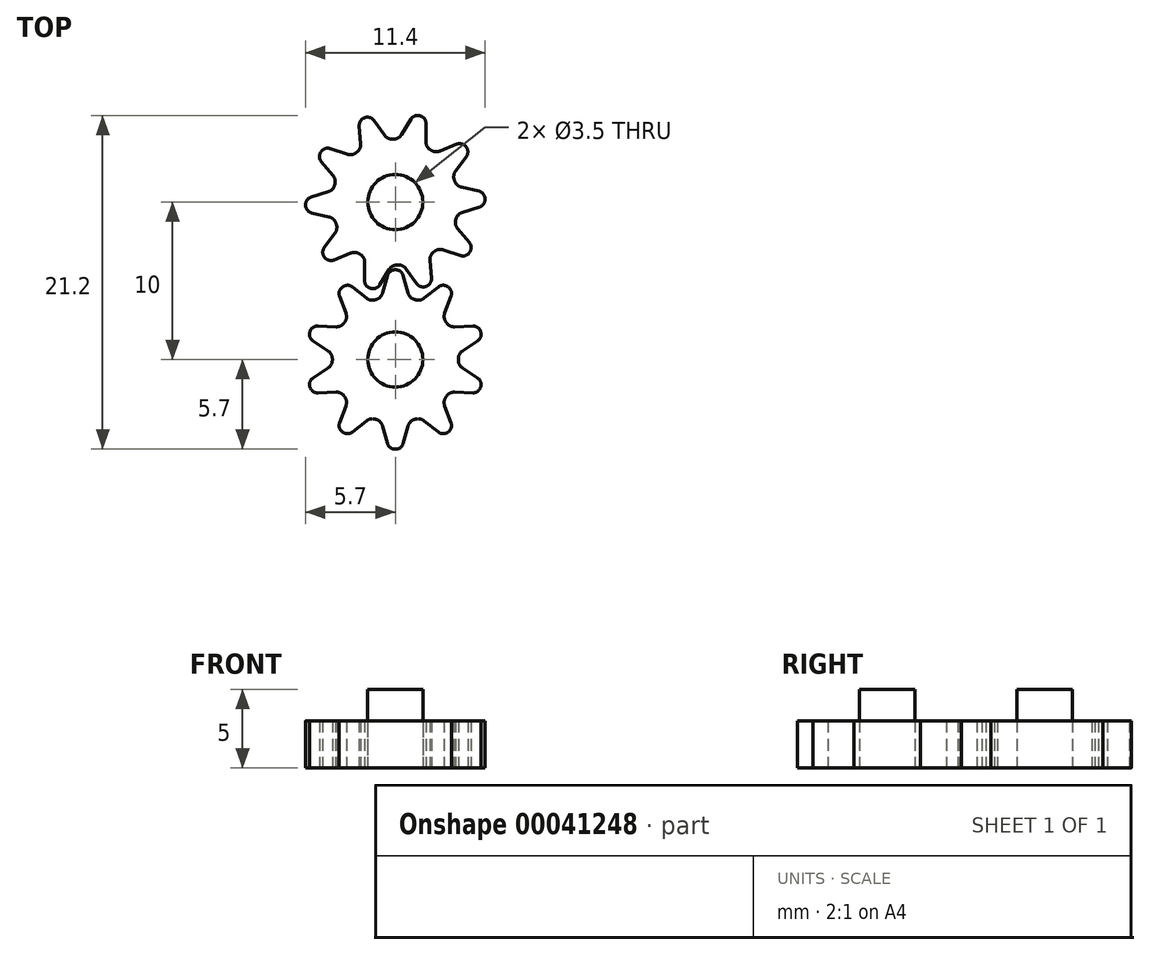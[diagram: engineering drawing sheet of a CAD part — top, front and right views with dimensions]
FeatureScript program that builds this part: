
annotation { "Feature Type Name" : "Feature", "Feature Type Description" : "" }
export const myFeature = defineFeature(function(context is Context, id is Id, definition is map)
    precondition{}
    {
        {
            var Q0;
            Q0=qCreatedBy(makeId("Top.planeOp"),FACE);
            var sketch = newSketch(context, id + "F0", { "sketchPlane" : qUnion([Q0])});
            skCircle(sketch, "E0", {"center": v(0, 0) * mm, "radius": 5 * mm, "construction": true});
            skLineSegment(sketch, "E1", {"start": v(0, 4) * mm, "end": v(0, 5.7) * mm, "construction": true});
            skArc(sketch, "E2", {"start": v(0.4, 5.69) * mm, "mid": v(0, 5.7) * mm, "end": v(-0.4, 5.69) * mm});
            skArc(sketch, "E3", {"start": v(-0.9, 3.9) * mm, "mid": v(0, -4) * mm, "end": v(0.9, 3.9) * mm});
            skLineSegment(sketch, "E4", {"start": v(0.4, 5.69) * mm, "end": v(0.9, 3.9) * mm});
            skLineSegment(sketch, "E5", {"start": v(-0.9, 3.9) * mm, "end": v(-0.4, 5.69) * mm});
            skPoint(sketch, "E6", {"position": v(0, 5) * mm});
            skLineSegment(sketch, "E7.1.0", {"start": v(-3.02, 4.84) * mm, "end": v(-1.56, 3.68) * mm});
            skPoint(sketch, "E7.1.1", {"position": v(-2.94, 4.05) * mm});
            skLineSegment(sketch, "E7.1.2", {"start": v(-3.02, 2.62) * mm, "end": v(-3.67, 4.36) * mm});
            skArc(sketch, "E7.1.3", {"start": v(-3.02, 4.84) * mm, "mid": v(-3.35, 4.61) * mm, "end": v(-3.67, 4.36) * mm});
            skLineSegment(sketch, "E7.1.4", {"start": v(-2.35, 3.24) * mm, "end": v(-3.35, 4.61) * mm, "construction": true});
            skLineSegment(sketch, "E7.2.0", {"start": v(-5.28, 2.14) * mm, "end": v(-3.43, 2.06) * mm});
            skPoint(sketch, "E7.2.1", {"position": v(-4.76, 1.55) * mm});
            skLineSegment(sketch, "E7.2.2", {"start": v(-3.98, 0.35) * mm, "end": v(-5.53, 1.38) * mm});
            skArc(sketch, "E7.2.3", {"start": v(-5.28, 2.14) * mm, "mid": v(-5.42, 1.76) * mm, "end": v(-5.53, 1.38) * mm});
            skLineSegment(sketch, "E7.2.4", {"start": v(-3.8, 1.24) * mm, "end": v(-5.42, 1.76) * mm, "construction": true});
            skLineSegment(sketch, "E7.3.0", {"start": v(-5.53, -1.38) * mm, "end": v(-3.98, -0.35) * mm});
            skPoint(sketch, "E7.3.1", {"position": v(-4.76, -1.55) * mm});
            skLineSegment(sketch, "E7.3.2", {"start": v(-3.43, -2.06) * mm, "end": v(-5.28, -2.14) * mm});
            skArc(sketch, "E7.3.3", {"start": v(-5.53, -1.38) * mm, "mid": v(-5.42, -1.76) * mm, "end": v(-5.28, -2.14) * mm});
            skLineSegment(sketch, "E7.3.4", {"start": v(-3.8, -1.24) * mm, "end": v(-5.42, -1.76) * mm, "construction": true});
            skLineSegment(sketch, "E7.4.0", {"start": v(-3.67, -4.36) * mm, "end": v(-3.02, -2.62) * mm});
            skPoint(sketch, "E7.4.1", {"position": v(-2.94, -4.05) * mm});
            skLineSegment(sketch, "E7.4.2", {"start": v(-1.56, -3.68) * mm, "end": v(-3.02, -4.84) * mm});
            skArc(sketch, "E7.4.3", {"start": v(-3.67, -4.36) * mm, "mid": v(-3.35, -4.61) * mm, "end": v(-3.02, -4.84) * mm});
            skLineSegment(sketch, "E7.4.4", {"start": v(-2.35, -3.24) * mm, "end": v(-3.35, -4.61) * mm, "construction": true});
            skLineSegment(sketch, "E7.5.0", {"start": v(-0.4, -5.69) * mm, "end": v(-0.9, -3.9) * mm});
            skPoint(sketch, "E7.5.1", {"position": v(0, -5) * mm});
            skLineSegment(sketch, "E7.5.2", {"start": v(0.9, -3.9) * mm, "end": v(0.4, -5.69) * mm});
            skArc(sketch, "E7.5.3", {"start": v(-0.4, -5.69) * mm, "mid": v(0, -5.7) * mm, "end": v(0.4, -5.69) * mm});
            skLineSegment(sketch, "E7.5.4", {"start": v(0, -4) * mm, "end": v(0, -5.7) * mm, "construction": true});
            skLineSegment(sketch, "E7.6.0", {"start": v(3.02, -4.84) * mm, "end": v(1.56, -3.68) * mm});
            skPoint(sketch, "E7.6.1", {"position": v(2.94, -4.05) * mm});
            skLineSegment(sketch, "E7.6.2", {"start": v(3.02, -2.62) * mm, "end": v(3.67, -4.36) * mm});
            skArc(sketch, "E7.6.3", {"start": v(3.02, -4.84) * mm, "mid": v(3.35, -4.61) * mm, "end": v(3.67, -4.36) * mm});
            skLineSegment(sketch, "E7.6.4", {"start": v(2.35, -3.24) * mm, "end": v(3.35, -4.61) * mm, "construction": true});
            skLineSegment(sketch, "E7.7.0", {"start": v(5.28, -2.14) * mm, "end": v(3.43, -2.06) * mm});
            skPoint(sketch, "E7.7.1", {"position": v(4.76, -1.55) * mm});
            skLineSegment(sketch, "E7.7.2", {"start": v(3.98, -0.35) * mm, "end": v(5.53, -1.38) * mm});
            skArc(sketch, "E7.7.3", {"start": v(5.28, -2.14) * mm, "mid": v(5.42, -1.76) * mm, "end": v(5.53, -1.38) * mm});
            skLineSegment(sketch, "E7.7.4", {"start": v(3.8, -1.24) * mm, "end": v(5.42, -1.76) * mm, "construction": true});
            skCircle(sketch, "E8", {"center": v(0, 0) * mm, "radius": 1.75 * mm});
            skLineSegment(sketch, "E9.2.8.0", {"start": v(5.53, 1.38) * mm, "end": v(3.98, 0.35) * mm});
            skPoint(sketch, "E9.3.8.0", {"position": v(4.76, 1.55) * mm});
            skLineSegment(sketch, "E9.4.8.0", {"start": v(3.43, 2.06) * mm, "end": v(5.28, 2.14) * mm});
            skArc(sketch, "E9.7.8.0", {"start": v(5.53, 1.38) * mm, "mid": v(5.42, 1.76) * mm, "end": v(5.28, 2.14) * mm});
            skLineSegment(sketch, "E9.11.8.0", {"start": v(3.8, 1.24) * mm, "end": v(5.42, 1.76) * mm, "construction": true});
            skLineSegment(sketch, "E10.2.9.0", {"start": v(3.67, 4.36) * mm, "end": v(3.02, 2.62) * mm});
            skPoint(sketch, "E10.3.9.0", {"position": v(2.94, 4.05) * mm});
            skLineSegment(sketch, "E10.4.9.0", {"start": v(1.56, 3.68) * mm, "end": v(3.02, 4.84) * mm});
            skArc(sketch, "E10.7.9.0", {"start": v(3.67, 4.36) * mm, "mid": v(3.35, 4.61) * mm, "end": v(3.02, 4.84) * mm});
            skLineSegment(sketch, "E10.11.9.0", {"start": v(2.35, 3.24) * mm, "end": v(3.35, 4.61) * mm, "construction": true});
            skSolve(sketch);
        }
        {
            var Q0;
            Q0 = qSketchRegion(id + "F0", true);
            extrude(context, id + "F1", {"entities" : qUnion([Q0]), "depth" : 3 * mm});
        }
        {
            var Q0;
            Q0=makeQuery(id+"F1.opExtrude","SWEPT_EDGE",EDGE,{"disambiguationData":[OSD([sQuery(id+"F0.wireOp",EDGE,"E2"),sQuery(id+"F0.wireOp",EDGE,"E4")])]});
            var Q1;
            Q1=makeQuery(id+"F1.opExtrude","SWEPT_EDGE",EDGE,{"disambiguationData":[OSD([sQuery(id+"F0.wireOp",EDGE,"E2"),sQuery(id+"F0.wireOp",EDGE,"E5")])]});
            var Q2;
            Q2=makeQuery(id+"F1.opExtrude","SWEPT_EDGE",EDGE,{"disambiguationData":[OSD([sQuery(id+"F0.wireOp",EDGE,"E7.1.0"),sQuery(id+"F0.wireOp",EDGE,"E7.1.3")])]});
            var Q3;
            Q3=makeQuery(id+"F1.opExtrude","SWEPT_EDGE",EDGE,{"disambiguationData":[OSD([sQuery(id+"F0.wireOp",EDGE,"E7.1.2"),sQuery(id+"F0.wireOp",EDGE,"E7.1.3")])]});
            var Q4;
            Q4=makeQuery(id+"F1.opExtrude","SWEPT_EDGE",EDGE,{"disambiguationData":[OSD([sQuery(id+"F0.wireOp",EDGE,"E9.4.8.0"),sQuery(id+"F0.wireOp",EDGE,"E9.7.8.0")])]});
            var Q5;
            Q5=makeQuery(id+"F1.opExtrude","SWEPT_EDGE",EDGE,{"disambiguationData":[OSD([sQuery(id+"F0.wireOp",EDGE,"E9.2.8.0"),sQuery(id+"F0.wireOp",EDGE,"E9.7.8.0")])]});
            var Q6;
            Q6=makeQuery(id+"F1.opExtrude","SWEPT_EDGE",EDGE,{"disambiguationData":[OSD([sQuery(id+"F0.wireOp",EDGE,"E7.7.2"),sQuery(id+"F0.wireOp",EDGE,"E7.7.3")])]});
            var Q7;
            Q7=makeQuery(id+"F1.opExtrude","SWEPT_EDGE",EDGE,{"disambiguationData":[OSD([sQuery(id+"F0.wireOp",EDGE,"E7.2.0"),sQuery(id+"F0.wireOp",EDGE,"E7.2.3")])]});
            var Q8;
            Q8=makeQuery(id+"F1.opExtrude","SWEPT_EDGE",EDGE,{"disambiguationData":[OSD([sQuery(id+"F0.wireOp",EDGE,"E7.7.0"),sQuery(id+"F0.wireOp",EDGE,"E7.7.3")])]});
            var Q9;
            Q9=makeQuery(id+"F1.opExtrude","SWEPT_EDGE",EDGE,{"disambiguationData":[OSD([sQuery(id+"F0.wireOp",EDGE,"E7.6.2"),sQuery(id+"F0.wireOp",EDGE,"E7.6.3")])]});
            var Q10;
            Q10=makeQuery(id+"F1.opExtrude","SWEPT_EDGE",EDGE,{"disambiguationData":[OSD([sQuery(id+"F0.wireOp",EDGE,"E7.6.0"),sQuery(id+"F0.wireOp",EDGE,"E7.6.3")])]});
            var Q11;
            Q11=makeQuery(id+"F1.opExtrude","SWEPT_EDGE",EDGE,{"disambiguationData":[OSD([sQuery(id+"F0.wireOp",EDGE,"E7.5.2"),sQuery(id+"F0.wireOp",EDGE,"E7.5.3")])]});
            var Q12;
            Q12=makeQuery(id+"F1.opExtrude","SWEPT_EDGE",EDGE,{"disambiguationData":[OSD([sQuery(id+"F0.wireOp",EDGE,"E7.5.0"),sQuery(id+"F0.wireOp",EDGE,"E7.5.3")])]});
            var Q13;
            Q13=makeQuery(id+"F1.opExtrude","SWEPT_EDGE",EDGE,{"disambiguationData":[OSD([sQuery(id+"F0.wireOp",EDGE,"E7.4.2"),sQuery(id+"F0.wireOp",EDGE,"E7.4.3")])]});
            var Q14;
            Q14=makeQuery(id+"F1.opExtrude","SWEPT_EDGE",EDGE,{"disambiguationData":[OSD([sQuery(id+"F0.wireOp",EDGE,"E7.4.0"),sQuery(id+"F0.wireOp",EDGE,"E7.4.3")])]});
            var Q15;
            Q15=makeQuery(id+"F1.opExtrude","SWEPT_EDGE",EDGE,{"disambiguationData":[OSD([sQuery(id+"F0.wireOp",EDGE,"E7.3.2"),sQuery(id+"F0.wireOp",EDGE,"E7.3.3")])]});
            var Q16;
            Q16=makeQuery(id+"F1.opExtrude","SWEPT_EDGE",EDGE,{"disambiguationData":[OSD([sQuery(id+"F0.wireOp",EDGE,"E7.3.0"),sQuery(id+"F0.wireOp",EDGE,"E7.3.3")])]});
            var Q17;
            Q17=makeQuery(id+"F1.opExtrude","SWEPT_EDGE",EDGE,{"disambiguationData":[OSD([sQuery(id+"F0.wireOp",EDGE,"E7.2.2"),sQuery(id+"F0.wireOp",EDGE,"E7.2.3")])]});
            var Q18;
            Q18=makeQuery(id+"F1.opExtrude","SWEPT_EDGE",EDGE,{"disambiguationData":[OSD([sQuery(id+"F0.wireOp",EDGE,"E10.2.9.0"),sQuery(id+"F0.wireOp",EDGE,"E10.7.9.0")])]});
            var Q19;
            Q19=makeQuery(id+"F1.opExtrude","SWEPT_EDGE",EDGE,{"disambiguationData":[OSD([sQuery(id+"F0.wireOp",EDGE,"E10.4.9.0"),sQuery(id+"F0.wireOp",EDGE,"E10.7.9.0")])]});
            fillet(context, id + "F2", {"entities" : qUnion([Q0, Q1, Q2, Q3, Q4, Q5, Q6, Q7, Q8, Q9, Q10, Q11, Q12, Q13, Q14, Q15, Q16, Q17, Q18, Q19]), "radius" : 0.5 * mm, "tangentPropagation" : true, "allowEdgeOverflow" : false});
        }
        {
            var Q0;
            Q0=makeQuery(id+"F1.opExtrude","SWEPT_EDGE",EDGE,{"disambiguationData":[OSD([sQuery(id+"F0.wireOp",EDGE,"E3"),sQuery(id+"F0.wireOp",EDGE,"E7.1.0")])]});
            var Q1;
            Q1=makeQuery(id+"F1.opExtrude","SWEPT_EDGE",EDGE,{"disambiguationData":[OSD([sQuery(id+"F0.wireOp",EDGE,"E3"),sQuery(id+"F0.wireOp",EDGE,"E4")])]});
            var Q2;
            Q2=makeQuery(id+"F1.opExtrude","SWEPT_EDGE",EDGE,{"disambiguationData":[OSD([sQuery(id+"F0.wireOp",EDGE,"E3"),sQuery(id+"F0.wireOp",EDGE,"E10.4.9.0")])]});
            var Q3;
            Q3=makeQuery(id+"F1.opExtrude","SWEPT_EDGE",EDGE,{"disambiguationData":[OSD([sQuery(id+"F0.wireOp",EDGE,"E3"),sQuery(id+"F0.wireOp",EDGE,"E5")])]});
            var Q4;
            Q4=makeQuery(id+"F1.opExtrude","SWEPT_EDGE",EDGE,{"disambiguationData":[OSD([sQuery(id+"F0.wireOp",EDGE,"E3"),sQuery(id+"F0.wireOp",EDGE,"E7.2.0")])]});
            var Q5;
            Q5=makeQuery(id+"F1.opExtrude","SWEPT_EDGE",EDGE,{"disambiguationData":[OSD([sQuery(id+"F0.wireOp",EDGE,"E3"),sQuery(id+"F0.wireOp",EDGE,"E7.1.2")])]});
            var Q6;
            Q6=makeQuery(id+"F1.opExtrude","SWEPT_EDGE",EDGE,{"disambiguationData":[OSD([sQuery(id+"F0.wireOp",EDGE,"E3"),sQuery(id+"F0.wireOp",EDGE,"E10.2.9.0")])]});
            var Q7;
            Q7=makeQuery(id+"F1.opExtrude","SWEPT_EDGE",EDGE,{"disambiguationData":[OSD([sQuery(id+"F0.wireOp",EDGE,"E3"),sQuery(id+"F0.wireOp",EDGE,"E9.4.8.0")])]});
            var Q8;
            Q8=makeQuery(id+"F1.opExtrude","SWEPT_EDGE",EDGE,{"disambiguationData":[OSD([sQuery(id+"F0.wireOp",EDGE,"E3"),sQuery(id+"F0.wireOp",EDGE,"E7.7.2")])]});
            var Q9;
            Q9=makeQuery(id+"F1.opExtrude","SWEPT_EDGE",EDGE,{"disambiguationData":[OSD([sQuery(id+"F0.wireOp",EDGE,"E3"),sQuery(id+"F0.wireOp",EDGE,"E9.2.8.0")])]});
            var Q10;
            Q10=makeQuery(id+"F1.opExtrude","SWEPT_EDGE",EDGE,{"disambiguationData":[OSD([sQuery(id+"F0.wireOp",EDGE,"E3"),sQuery(id+"F0.wireOp",EDGE,"E7.6.2")])]});
            var Q11;
            Q11=makeQuery(id+"F1.opExtrude","SWEPT_EDGE",EDGE,{"disambiguationData":[OSD([sQuery(id+"F0.wireOp",EDGE,"E3"),sQuery(id+"F0.wireOp",EDGE,"E7.7.0")])]});
            var Q12;
            Q12=makeQuery(id+"F1.opExtrude","SWEPT_EDGE",EDGE,{"disambiguationData":[OSD([sQuery(id+"F0.wireOp",EDGE,"E3"),sQuery(id+"F0.wireOp",EDGE,"E7.5.2")])]});
            var Q13;
            Q13=makeQuery(id+"F1.opExtrude","SWEPT_EDGE",EDGE,{"disambiguationData":[OSD([sQuery(id+"F0.wireOp",EDGE,"E3"),sQuery(id+"F0.wireOp",EDGE,"E7.6.0")])]});
            var Q14;
            Q14=makeQuery(id+"F1.opExtrude","SWEPT_EDGE",EDGE,{"disambiguationData":[OSD([sQuery(id+"F0.wireOp",EDGE,"E3"),sQuery(id+"F0.wireOp",EDGE,"E7.5.0")])]});
            var Q15;
            Q15=makeQuery(id+"F1.opExtrude","SWEPT_EDGE",EDGE,{"disambiguationData":[OSD([sQuery(id+"F0.wireOp",EDGE,"E3"),sQuery(id+"F0.wireOp",EDGE,"E7.4.2")])]});
            var Q16;
            Q16=makeQuery(id+"F1.opExtrude","SWEPT_EDGE",EDGE,{"disambiguationData":[OSD([sQuery(id+"F0.wireOp",EDGE,"E3"),sQuery(id+"F0.wireOp",EDGE,"E7.4.0")])]});
            var Q17;
            Q17=makeQuery(id+"F1.opExtrude","SWEPT_EDGE",EDGE,{"disambiguationData":[OSD([sQuery(id+"F0.wireOp",EDGE,"E3"),sQuery(id+"F0.wireOp",EDGE,"E7.3.2")])]});
            var Q18;
            Q18=makeQuery(id+"F1.opExtrude","SWEPT_EDGE",EDGE,{"disambiguationData":[OSD([sQuery(id+"F0.wireOp",EDGE,"E3"),sQuery(id+"F0.wireOp",EDGE,"E7.3.0")])]});
            var Q19;
            Q19=makeQuery(id+"F1.opExtrude","SWEPT_EDGE",EDGE,{"disambiguationData":[OSD([sQuery(id+"F0.wireOp",EDGE,"E3"),sQuery(id+"F0.wireOp",EDGE,"E7.2.2")])]});
            fillet(context, id + "F3", {"entities" : qUnion([Q0, Q1, Q2, Q3, Q4, Q5, Q6, Q7, Q8, Q9, Q10, Q11, Q12, Q13, Q14, Q15, Q16, Q17, Q18, Q19]), "radius" : 0.6 * mm, "tangentPropagation" : true, "allowEdgeOverflow" : false});
        }
        {
            var Q0;
            Q0=qCreatedBy(makeId("Right.planeOp"),FACE);
            var sketch = newSketch(context, id + "F4", { "sketchPlane" : qUnion([Q0])});
            skLineSegment(sketch, "E11", {"start": v(0, 0) * mm, "end": v(0, 14.37) * mm, "construction": true});
            skSolve(sketch);
        }
        {
            var Q0;
            Q0=makeQuery(id+"F1.opExtrude","SWEPT_BODY",BODY,{"disambiguationData":[OSD([sQuery(id+"F0.wireOp",EDGE,"E2"),sQuery(id+"F0.wireOp",EDGE,"E3"),sQuery(id+"F0.wireOp",EDGE,"E4"),sQuery(id+"F0.wireOp",EDGE,"E5")])]});
            var Q1;
            Q1=sQuery(id+"F4.wireOp",EDGE,"E11");
            transform(context, id + "F5", {"entities" : qUnion([Q0]), "transformType" : TransformType.ROTATION, "transformAxis" : qUnion([Q1]), "angle" : 200 * degree, "makeCopy" : true});
        }
        {
            var Q0;
            Q0=makeQuery(id+"F5.opPattern","COPY",BODY,{"derivedFrom":makeQuery(id+"F1.opExtrude","SWEPT_BODY",BODY,{"disambiguationData":[OSD([sQuery(id+"F0.wireOp",EDGE,"E2"),sQuery(id+"F0.wireOp",EDGE,"E3"),sQuery(id+"F0.wireOp",EDGE,"E4"),sQuery(id+"F0.wireOp",EDGE,"E5")])]}),"instanceName":"1"});
            transform(context, id + "F6", {"entities" : qUnion([Q0]), "transformType" : TransformType.TRANSLATION_3D, "dx" : 0 * mm, "dy" : 10 * mm, "dz" : 0 * mm, "makeCopy" : false});
        }
        {
            var Q0;
            Q0=qCreatedBy(makeId("Top.planeOp"),FACE);
            var sketch = newSketch(context, id + "F7", { "sketchPlane" : qUnion([Q0])});
            skCircle(sketch, "E12", {"center": v(0, 0) * mm, "radius": 1.75 * mm});
            skCircle(sketch, "E13", {"center": v(0, 10) * mm, "radius": 1.75 * mm});
            skSolve(sketch);
        }
        {
            var Q0;
            Q0 = qSketchRegion(id + "F7", true);
            extrude(context, id + "F8", {"entities" : qUnion([Q0]), "depth" : 5 * mm});
        }
    });
